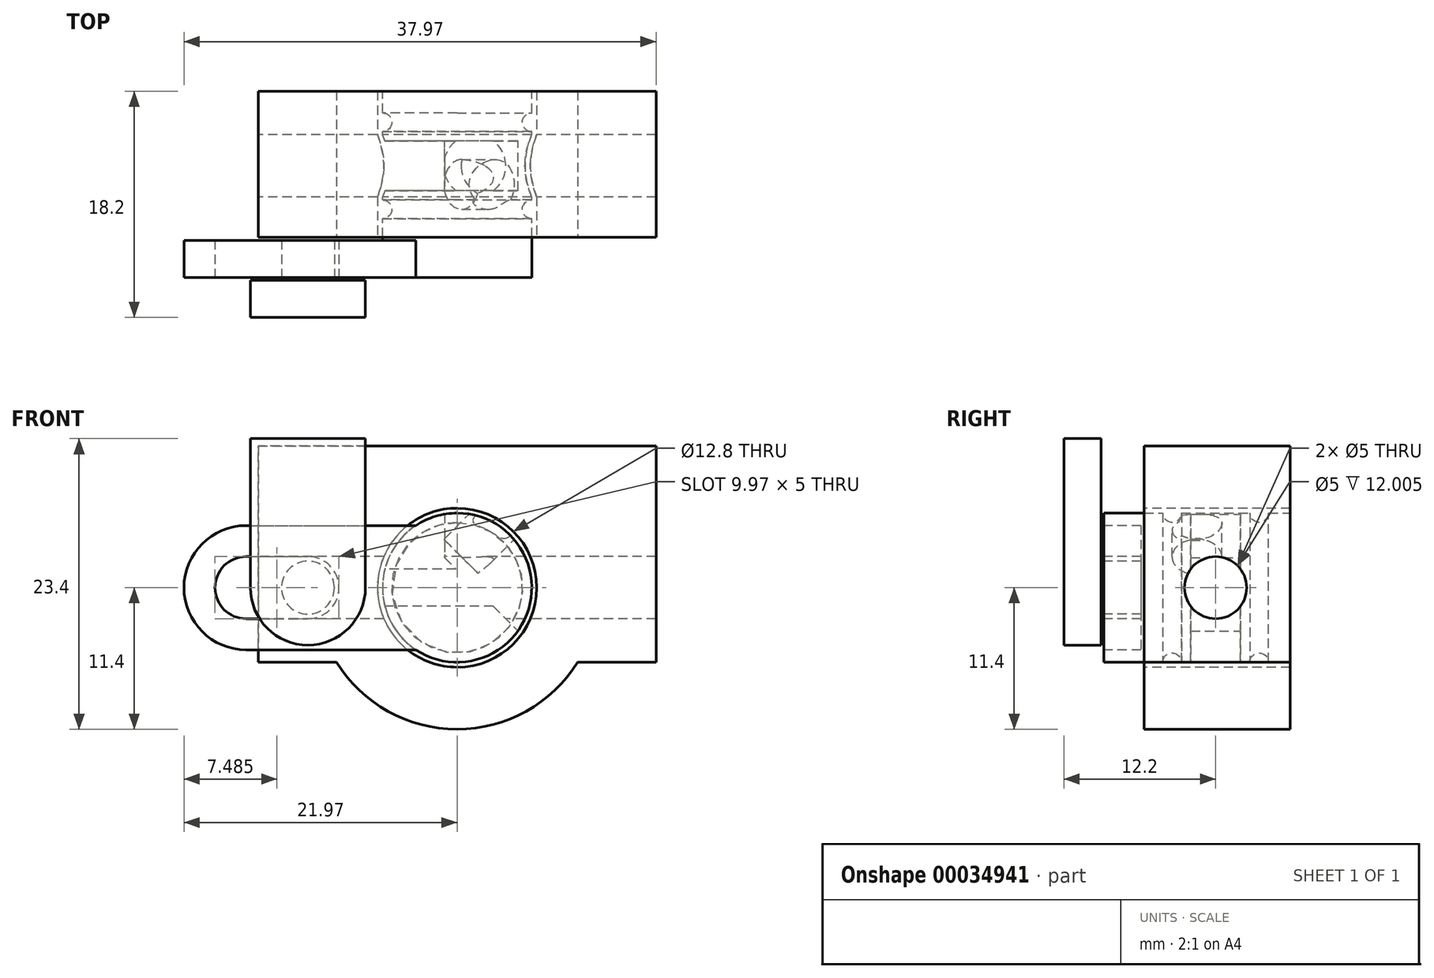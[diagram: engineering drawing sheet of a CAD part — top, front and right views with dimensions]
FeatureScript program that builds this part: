
annotation { "Feature Type Name" : "Feature", "Feature Type Description" : "" }
export const myFeature = defineFeature(function(context is Context, id is Id, definition is map)
    precondition{}
    {
        {
            var Q0;
            Q0=qCreatedBy(makeId("Front.planeOp"),FACE);
            var sketch = newSketch(context, id + "F0", { "sketchPlane" : qUnion([Q0])});
            skLineSegment(sketch, "E0", {"start": v(0, 25.52) * mm, "end": v(0, 0) * mm, "construction": true});
            skLineSegment(sketch, "E1", {"start": v(0, 0) * mm, "end": v(34.8, 0) * mm, "construction": true});
            skCircle(sketch, "E2", {"center": v(0, 0) * mm, "radius": 6 * mm});
            skSolve(sketch);
        }
        {
            var Q0;
            Q0=makeQuery(id+"F0.imprint","IMPRINT",FACE,{"disambiguationData":[TD([[makeQuery(id+"F0.imprint","IMPRINT",EDGE,{"derivedFrom":sQuery(id+"F0.wireOp",EDGE,"E2")}),1.0]])]});
            extrude(context, id + "F1", {"entities" : qUnion([Q0]), "endBound" : BoundingType.SYMMETRIC, "depth" : 15 * mm});
        }
        {
            var Q0;
            Q0=qCreatedBy(makeId("Front.planeOp"),FACE);
            var sketch = newSketch(context, id + "F2", { "sketchPlane" : qUnion([Q0])});
            skLineSegment(sketch, "E3", {"start": v(0, 10.1) * mm, "end": v(0, 0) * mm, "construction": true});
            skLineSegment(sketch, "E4", {"start": v(0, 0) * mm, "end": v(-16.97, 0) * mm, "construction": true});
            skLineSegment(sketch, "E5", {"start": v(0, 0) * mm, "end": v(-12, 12) * mm, "construction": true});
            skLineSegment(sketch, "E6", {"start": v(-12, 12) * mm, "end": v(-12, -12) * mm, "construction": true});
            skLineSegment(sketch, "E7", {"start": v(-12, -12) * mm, "end": v(0, 0) * mm, "construction": true});
            skLineSegment(sketch, "E8", {"start": v(0, 0) * mm, "end": v(12, 12) * mm, "construction": true});
            skSolve(sketch);
        }
        {
            var Q0;
            Q0=makeQuery(id+"F1.opExtrude","CAP_FACE",FACE,{"disambiguationData":[OSD([sQuery(id+"F0.wireOp",EDGE,"E2")])],"isStart":false});
            var sketch = newSketch(context, id + "F3", { "sketchPlane" : qUnion([Q0])});
            skArc(sketch, "E9", {"start": v(-16.97, 2.5) * mm, "mid": v(-19.47, 0) * mm, "end": v(-16.97, -2.5) * mm});
            skLineSegment(sketch, "E10", {"start": v(-16.97, 2.5) * mm, "end": v(-12, 2.5) * mm});
            skLineSegment(sketch, "E11.0", {"start": v(0, 0) * mm, "end": v(-16.97, 0) * mm, "construction": true});
            skLineSegment(sketch, "E12.MirrorCS", {"start": v(-16.97, -2.5) * mm, "end": v(-12, -2.5) * mm});
            skArc(sketch, "E13", {"start": v(-12, -2.5) * mm, "mid": v(-9.5, 0) * mm, "end": v(-12, 2.5) * mm});
            skLineSegment(sketch, "E14.0", {"start": v(-16.97, 5) * mm, "end": v(-3.32, 5) * mm});
            skArc(sketch, "E14.1", {"start": v(-16.97, 5) * mm, "mid": v(-21.97, 0) * mm, "end": v(-16.97, -5) * mm});
            skLineSegment(sketch, "E15.MirrorCS", {"start": v(-16.97, -5) * mm, "end": v(-3.32, -5) * mm});
            skArc(sketch, "E16.0", {"start": v(-3.32, 5) * mm, "mid": v(-6, 0) * mm, "end": v(-3.32, -5) * mm});
            skSolve(sketch);
        }
        {
            var Q0;
            Q0 = qSketchRegion(id + "F3", true);
            extrude(context, id + "F4", {"entities" : qUnion([Q0]), "operationType" : NewBodyOperationType.ADD, "oppositeDirection" : true, "depth" : 3 * mm});
        }
        {
            var Q0;
            Q0=sQuery(id+"F2.wireOp",VERTEX,"E8.end");
            var Q1;
            Q1=sQuery(id+"F2.wireOp",EDGE,"E8");
            cPlane(context, id + "F5", {"entities" : qUnion([Q0, Q1]), "cplaneType" : CPlaneType.LINE_POINT, "offset" : 1 * mm, "width" : 150 * mm, "height" : 150 * mm});
        }
        {
            var Q0;
            Q0=qCreatedBy(id+"F5.planeOp",FACE);
            var sketch = newSketch(context, id + "F6", { "sketchPlane" : qUnion([Q0])});
            skLineSegment(sketch, "E17", {"start": v(0, 0) * mm, "end": v(-11.1, 0) * mm, "construction": true});
            skCircle(sketch, "E18", {"center": v(0, 1.5) * mm, "radius": 2 * mm});
            skSolve(sketch);
        }
        {
            var Q0;
            Q0=qCreatedBy(id+"F5.planeOp",FACE);
            var Q1;
            Q1=sQuery(id+"F2.wireOp",VERTEX,"E5.start");
            cPlane(context, id + "F7", {"entities" : qUnion([Q0, Q1]), "cplaneType" : CPlaneType.PLANE_POINT, "offset" : 150 * mm, "width" : 150 * mm, "height" : 150 * mm});
        }
        {
            var Q0;
            Q0=qCreatedBy(id+"F7.planeOp",FACE);
            cPlane(context, id + "F8", {"entities" : qUnion([Q0]), "cplaneType" : CPlaneType.OFFSET, "offset" : 2 * mm, "width" : 150 * mm, "height" : 150 * mm});
        }
        {
            var Q0;
            Q0 = qSketchRegion(id + "F6", true);
            var Q1;
            Q1=qCreatedBy(id+"F8.planeOp",FACE);
            extrude(context, id + "F9", {"entities" : qUnion([Q0]), "operationType" : NewBodyOperationType.REMOVE, "endBound" : BoundingType.UP_TO_SURFACE, "oppositeDirection" : true, "endBoundEntityFace" : qUnion([Q1]), "depth" : 25 * mm});
        }
        {
            var Q0;
            Q0=qCreatedBy(makeId("Top.planeOp"),FACE);
            var sketch = newSketch(context, id + "F10", { "sketchPlane" : qUnion([Q0])});
            skLineSegment(sketch, "E19", {"start": v(0, 0) * mm, "end": v(0, 6.7) * mm, "construction": true});
            skCircle(sketch, "E20", {"center": v(-6, 5) * mm, "radius": 0.75 * mm});
            skCircle(sketch, "E21", {"center": v(-6, -2) * mm, "radius": 0.75 * mm});
            skSolve(sketch);
        }
        {
            var Q0;
            Q0 = qSketchRegion(id + "F10", true);
            var Q1;
            Q1=sQuery(id+"F10.wireOp",EDGE,"E19");
            revolve(context, id + "F11", {"operationType" : NewBodyOperationType.REMOVE, "entities" : qUnion([Q0]), "axis" : qUnion([Q1]), "revolveType" : RevolveType.FULL, "oppositeDirection" : true});
        }
        {
            var Q0;
            Q0=makeQuery(id+"F4.boolean.opBoolean","MERGE",FACE,{"derivedFrom":[makeQuery(id+"F1.opExtrude","CAP_FACE",FACE,{"disambiguationData":[OSD([sQuery(id+"F0.wireOp",EDGE,"E2")])],"isStart":false}),makeQuery(id+"F4.opExtrude","CAP_FACE",FACE,{"disambiguationData":[OSD([sQuery(id+"F3.wireOp",EDGE,"E9"),sQuery(id+"F3.wireOp",EDGE,"E10"),sQuery(id+"F3.wireOp",EDGE,"E12.MirrorCS"),sQuery(id+"F3.wireOp",EDGE,"E13"),sQuery(id+"F3.wireOp",EDGE,"E14.0"),sQuery(id+"F3.wireOp",EDGE,"E14.1"),sQuery(id+"F3.wireOp",EDGE,"E15.MirrorCS"),sQuery(id+"F3.wireOp",EDGE,"E16.0")])],"isStart":true})]});
            cPlane(context, id + "F12", {"entities" : qUnion([Q0]), "cplaneType" : CPlaneType.OFFSET, "offset" : .2 * mm, "width" : 150 * mm, "height" : 150 * mm});
        }
        {
            var Q0;
            Q0=qCreatedBy(id+"F12.planeOp",FACE);
            var sketch = newSketch(context, id + "F13", { "sketchPlane" : qUnion([Q0])});
            skLineSegment(sketch, "E22.bottom", {"start": v(-16.62, 12) * mm, "end": v(-7.38, 12) * mm});
            skLineSegment(sketch, "E22.left", {"start": v(-7.38, 12) * mm, "end": v(-7.38, 0) * mm});
            skLineSegment(sketch, "E22.right", {"start": v(-16.62, 12) * mm, "end": v(-16.62, 0) * mm});
            skLineSegment(sketch, "E23.0", {"start": v(-12, 12) * mm, "end": v(-12, -12) * mm, "construction": true});
            skCircle(sketch, "E24", {"center": v(-12, 0) * mm, "radius": 2.12 * mm, "construction": true});
            skArc(sketch, "E25", {"start": v(-16.63, 0) * mm, "mid": v(-12, -4.63) * mm, "end": v(-7.37, 0) * mm});
            skSolve(sketch);
        }
        {
            var Q0;
            Q0 = qSketchRegion(id + "F13", true);
            extrude(context, id + "F14", {"entities" : qUnion([Q0]), "depth" : 3 * mm});
        }
        {
            var Q0;
            Q0=makeQuery(id+"F14.opExtrude","CAP_FACE",FACE,{"disambiguationData":[OSD([sQuery(id+"F13.wireOp",EDGE,"E22.bottom"),sQuery(id+"F13.wireOp",EDGE,"E22.left"),sQuery(id+"F13.wireOp",EDGE,"E22.right"),sQuery(id+"F13.wireOp",EDGE,"E25")])],"isStart":true});
            var sketch = newSketch(context, id + "F15", { "sketchPlane" : qUnion([Q0])});
            skCircle(sketch, "E26.0", {"center": v(12, 0) * mm, "radius": 2.12 * mm});
            skSolve(sketch);
        }
        {
            var Q0;
            Q0 = qSketchRegion(id + "F15", true);
            extrude(context, id + "F16", {"entities" : qUnion([Q0]), "operationType" : NewBodyOperationType.ADD, "depth" : 3.2 * mm});
        }
        {
            var Q0;
            Q0=makeQuery(id+"F1.opExtrude","CAP_FACE",FACE,{"disambiguationData":[OSD([sQuery(id+"F0.wireOp",EDGE,"E2")])],"isStart":true});
            cPlane(context, id + "F17", {"entities" : qUnion([Q0]), "cplaneType" : CPlaneType.OFFSET, "offset" : 6 * mm, "oppositeDirection" : true, "width" : 150 * mm, "height" : 150 * mm});
        }
        {
            var Q0;
            Q0=qCreatedBy(id+"F17.planeOp",FACE);
            var sketch = newSketch(context, id + "F18", { "sketchPlane" : qUnion([Q0])});
            skLineSegment(sketch, "E27", {"start": v(1, 6.17) * mm, "end": v(1, 2.41) * mm});
            skLineSegment(sketch, "E28", {"start": v(1, 2.41) * mm, "end": v(-5.07, -3.66) * mm});
            skArc(sketch, "E29", {"start": v(-5.07, -3.66) * mm, "mid": v(5.32, -3.28) * mm, "end": v(1, 6.17) * mm});
            skSolve(sketch);
        }
        {
            var Q0;
            Q0 = qSketchRegion(id + "F18", true);
            extrude(context, id + "F19", {"entities" : qUnion([Q0]), "operationType" : NewBodyOperationType.REMOVE, "endBound" : BoundingType.SYMMETRIC, "oppositeDirection" : true, "depth" : 4 * mm});
        }
        {
            var Q0;
            Q0=makeQuery(id+"F4.opExtrude","CAP_FACE",FACE,{"disambiguationData":[OSD([sQuery(id+"F3.wireOp",EDGE,"E9"),sQuery(id+"F3.wireOp",EDGE,"E10"),sQuery(id+"F3.wireOp",EDGE,"E12.MirrorCS"),sQuery(id+"F3.wireOp",EDGE,"E13"),sQuery(id+"F3.wireOp",EDGE,"E14.0"),sQuery(id+"F3.wireOp",EDGE,"E14.1"),sQuery(id+"F3.wireOp",EDGE,"E15.MirrorCS"),sQuery(id+"F3.wireOp",EDGE,"E16.0")])],"isStart":false});
            cPlane(context, id + "F20", {"entities" : qUnion([Q0]), "cplaneType" : CPlaneType.OFFSET, "offset" : .25 * mm, "width" : 150 * mm, "height" : 150 * mm});
        }
        {
            var Q0;
            Q0=qCreatedBy(id+"F20.planeOp",FACE);
            var sketch = newSketch(context, id + "F21", { "sketchPlane" : qUnion([Q0])});
            skLineSegment(sketch, "E30", {"start": v(-16, 11.4) * mm, "end": v(-16, -6) * mm});
            skLineSegment(sketch, "E31", {"start": v(-16, 11.4) * mm, "end": v(16, 11.4) * mm});
            skCircle(sketch, "E32", {"center": v(0, 0) * mm, "radius": 11.4 * mm, "construction": true});
            skLineSegment(sketch, "E33", {"start": v(-16, -6) * mm, "end": v(-9.7, -6) * mm});
            skLineSegment(sketch, "E34.0", {"start": v(0, 0) * mm, "end": v(12, 12) * mm, "construction": true});
            skLineSegment(sketch, "E35.MirrorCS", {"start": v(16, -6) * mm, "end": v(9.7, -6) * mm});
            skArc(sketch, "E36", {"start": v(-9.7, -6) * mm, "mid": v(0, -11.4) * mm, "end": v(9.7, -6) * mm});
            skCircle(sketch, "E37", {"center": v(0, 0) * mm, "radius": 6.4 * mm});
            skLineSegment(sketch, "E38", {"start": v(16, 11.4) * mm, "end": v(16, -6) * mm});
            skSolve(sketch);
        }
        {
            var Q0;
            Q0 = qSketchRegion(id + "F21", true);
            var Q1;
            Q1=makeQuery(id+"F1.opExtrude","CAP_FACE",FACE,{"disambiguationData":[OSD([sQuery(id+"F0.wireOp",EDGE,"E2")])],"isStart":true});
            extrude(context, id + "F22", {"entities" : qUnion([Q0]), "endBound" : BoundingType.UP_TO_SURFACE, "endBoundEntityFace" : qUnion([Q1]), "depth" : 25 * mm});
        }
        {
            var Q0;
            Q0=makeQuery(id+"F22.opExtrude","SWEPT_FACE",FACE,{"disambiguationData":[OSD([sQuery(id+"F21.wireOp",EDGE,"E38")])]});
            var sketch = newSketch(context, id + "F23", { "sketchPlane" : qUnion([Q0])});
            skCircle(sketch, "E39", {"center": v(-1.5, 0) * mm, "radius": 2.5 * mm});
            skSolve(sketch);
        }
        {
            var Q0;
            Q0 = qSketchRegion(id + "F23", true);
            extrude(context, id + "F24", {"entities" : qUnion([Q0]), "operationType" : NewBodyOperationType.REMOVE, "endBound" : BoundingType.THROUGH_ALL, "oppositeDirection" : true, "depth" : 25 * mm});
        }
    });
